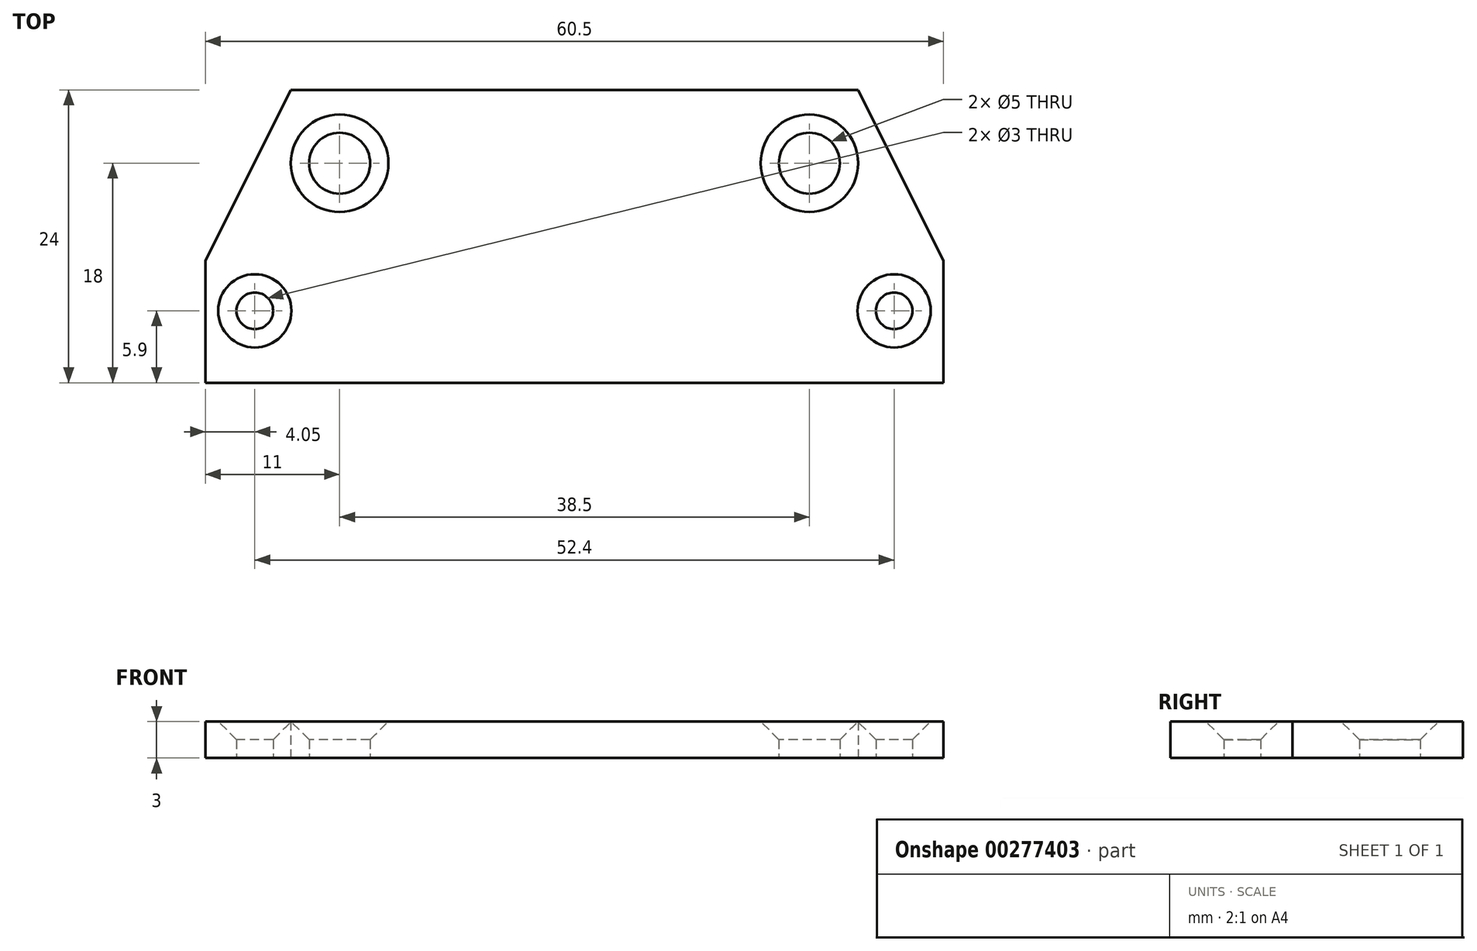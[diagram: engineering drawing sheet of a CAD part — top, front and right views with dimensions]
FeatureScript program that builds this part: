
annotation { "Feature Type Name" : "Feature", "Feature Type Description" : "" }
export const myFeature = defineFeature(function(context is Context, id is Id, definition is map)
    precondition{}
    {
        {
            var Q0;
            Q0=qCreatedBy(makeId("Top.planeOp"),FACE);
            var sketch = newSketch(context, id + "F0", { "sketchPlane" : qUnion([Q0])});
            skLineSegment(sketch, "E0.bottom", {"start": v(-30.25, 59.5) * mm, "end": v(30.25, 59.5) * mm});
            skCircle(sketch, "E1", {"center": v(-26.2, 55.4) * mm, "radius": 1.5 * mm});
            skCircle(sketch, "E2.MirrorC", {"center": v(26.2, 55.4) * mm, "radius": 1.5 * mm});
            skLineSegment(sketch, "E3.bottom", {"start": v(30.25, 49.5) * mm, "end": v(-30.25, 49.5) * mm});
            skLineSegment(sketch, "E4", {"start": v(-30.25, 59.5) * mm, "end": v(-30.25, 49.5) * mm});
            skLineSegment(sketch, "E5", {"start": v(30.25, 59.5) * mm, "end": v(30.25, 49.5) * mm});
            skLineSegment(sketch, "E6", {"start": v(-30.25, 59.5) * mm, "end": v(-23.25, 73.5) * mm});
            skLineSegment(sketch, "E7", {"start": v(30.25, 59.5) * mm, "end": v(23.25, 73.5) * mm});
            skCircle(sketch, "E8", {"center": v(-19.25, 67.5) * mm, "radius": 2.5 * mm});
            skLineSegment(sketch, "E9", {"start": v(-23.25, 73.5) * mm, "end": v(23.25, 73.5) * mm});
            skCircle(sketch, "E10.MirrorC", {"center": v(19.25, 67.5) * mm, "radius": 2.5 * mm});
            skSolve(sketch);
        }
        {
            var Q0;
            Q0=makeQuery(id+"F0.imprint","IMPRINT",FACE,{"disambiguationData":[TD([[makeQuery(id+"F0.imprint","IMPRINT",EDGE,{"derivedFrom":sQuery(id+"F0.wireOp",EDGE,"E0.bottom")}),-1.0]])]});
            var Q1;
            Q1=makeQuery(id+"F0.imprint","IMPRINT",FACE,{"disambiguationData":[TD([[makeQuery(id+"F0.imprint","IMPRINT",EDGE,{"derivedFrom":sQuery(id+"F0.wireOp",EDGE,"E0.bottom")}),1.0]])]});
            var Q2;
            Q2=makeQuery(id+"F0.imprint","IMPRINT",FACE,{"disambiguationData":[TD([[makeQuery(id+"F0.imprint","IMPRINT",EDGE,{"derivedFrom":sQuery(id+"F0.wireOp",EDGE,"E0.top")}),-1.0]])]});
            var Q3;
            Q3=makeQuery(id+"F0.imprint","IMPRINT",FACE,{"disambiguationData":[TD([[makeQuery(id+"F0.imprint","IMPRINT",EDGE,{"derivedFrom":sQuery(id+"F0.wireOp",EDGE,"E1")}),-1.0]])]});
            var Q4;
            Q4=makeQuery(id+"F0.imprint","IMPRINT",FACE,{"disambiguationData":[TD([[makeQuery(id+"F0.imprint","IMPRINT",EDGE,{"derivedFrom":sQuery(id+"F0.wireOp",EDGE,"0136b41d-0119-4568-9ff4-ad2a73c5a5d40.MirrorC")}),-1.0]])]});
            var Q5;
            Q5=makeQuery(id+"F0.imprint","IMPRINT",FACE,{"disambiguationData":[TD([[makeQuery(id+"F0.imprint","IMPRINT",EDGE,{"derivedFrom":sQuery(id+"F0.wireOp",EDGE,"963c80e6-d9c7-4d8a-a2e0-e8238a1a8c6b2.MirrorC")}),1.0]])]});
            var Q6;
            Q6=makeQuery(id+"F0.imprint","IMPRINT",FACE,{"disambiguationData":[TD([[makeQuery(id+"F0.imprint","IMPRINT",EDGE,{"derivedFrom":sQuery(id+"F0.wireOp",EDGE,"963c80e6-d9c7-4d8a-a2e0-e8238a1a8c6b0.MirrorC")}),-1.0]])]});
            var Q7;
            {var subQ1=sQuery(id+"F0.wireOp",EDGE,"E0.top");Q7=makeQuery(id+"F0.imprint","IMPRINT",FACE,{"disambiguationData":[TD([[makeQuery(id+"F0.imprint","IMPRINT",EDGE,{"derivedFrom":subQ1}),1.0]])]});}
            extrude(context, id + "F1", {"entities" : qUnion([Q0, Q1, Q2, Q3, Q4, Q5, Q6, Q7]), "depth" : 3 * mm});
        }
        {
            var Q0;
            Q0=makeQuery(id+"F1.opExtrude","CAP_EDGE",EDGE,{"disambiguationData":[OSD([sQuery(id+"F0.wireOp",EDGE,"E1")])],"isStart":false});
            var Q1;
            Q1=makeQuery(id+"F1.opExtrude","CAP_EDGE",EDGE,{"disambiguationData":[OSD([sQuery(id+"F0.wireOp",EDGE,"E2.MirrorC")])],"isStart":false});
            var Q2;
            Q2=makeQuery(id+"F1.opExtrude","CAP_EDGE",EDGE,{"disambiguationData":[OSD([sQuery(id+"F0.wireOp",EDGE,"963c80e6-d9c7-4d8a-a2e0-e8238a1a8c6b0.MirrorC")])],"isStart":false});
            var Q3;
            Q3=makeQuery(id+"F1.opExtrude","CAP_EDGE",EDGE,{"disambiguationData":[OSD([sQuery(id+"F0.wireOp",EDGE,"963c80e6-d9c7-4d8a-a2e0-e8238a1a8c6b2.MirrorC")])],"isStart":false});
            chamfer(context, id + "F2", {"entities" : qUnion([Q0, Q1, Q2, Q3]), "width" : 1.5 * mm, "tangentPropagation" : true});
        }
        {
            var Q0;
            Q0=makeQuery(id+"F1.opExtrude","CAP_EDGE",EDGE,{"disambiguationData":[OSD([sQuery(id+"F0.wireOp",EDGE,"E10.MirrorC")])],"isStart":false});
            var Q1;
            Q1=makeQuery(id+"F1.opExtrude","CAP_EDGE",EDGE,{"disambiguationData":[OSD([sQuery(id+"F0.wireOp",EDGE,"E8")])],"isStart":false});
            chamfer(context, id + "F3", {"entities" : qUnion([Q0, Q1]), "width" : 1.5 * mm, "tangentPropagation" : true});
        }
    });
